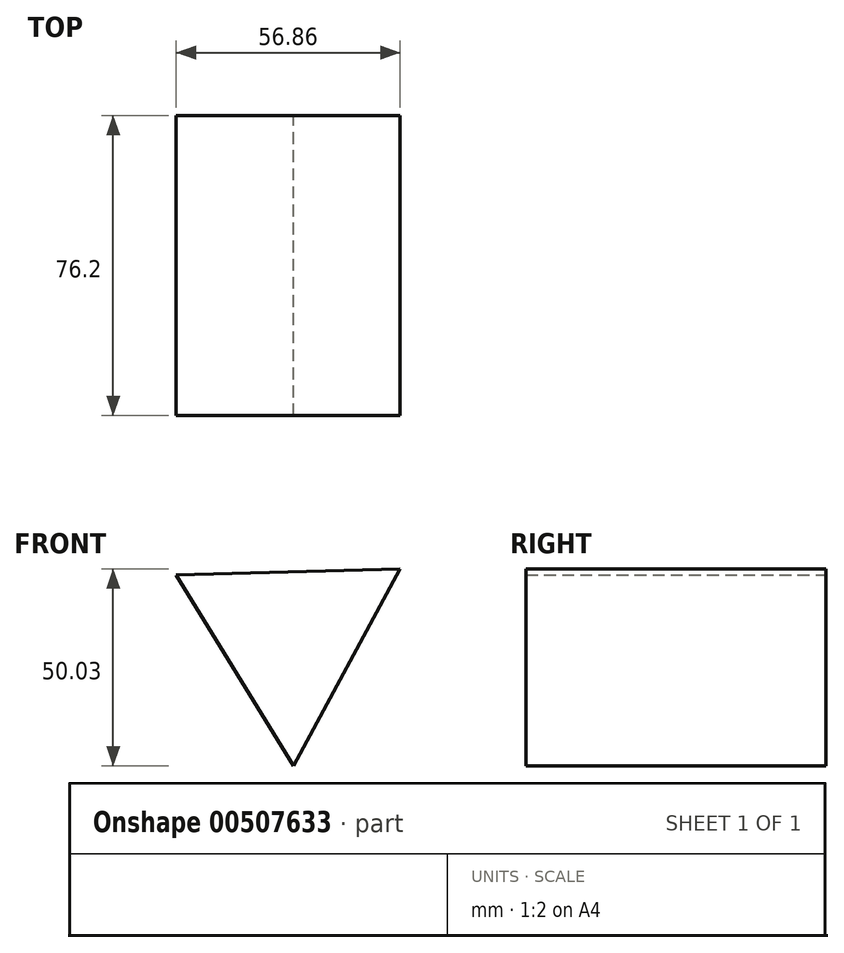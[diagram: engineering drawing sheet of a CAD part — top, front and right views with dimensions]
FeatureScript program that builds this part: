
annotation { "Feature Type Name" : "Feature", "Feature Type Description" : "" }
export const myFeature = defineFeature(function(context is Context, id is Id, definition is map)
    precondition{}
    {
        {
            var Q0;
            Q0=qCreatedBy(makeId("Front.planeOp"),FACE);
            var sketch = newSketch(context, id + "F0", { "sketchPlane" : qUnion([Q0])});
            skCircle(sketch, "E0.cCircle", {"center": v(0, 0) * mm, "radius": 16.42 * mm, "construction": true});
            skLineSegment(sketch, "E0.0", {"start": v(0.9, -32.83) * mm, "end": v(-28.88, 15.63) * mm});
            skLineSegment(sketch, "E0.1", {"start": v(-28.88, 15.63) * mm, "end": v(27.98, 17.2) * mm});
            skLineSegment(sketch, "E0.2", {"start": v(27.98, 17.2) * mm, "end": v(0.9, -32.83) * mm});
            skPoint(sketch, "E0.0.midPoint", {"position": v(-14, -8.6) * mm});
            skSolve(sketch);
        }
        {
            var Q0;
            Q0=makeQuery(id+"F0.imprint","IMPRINT",FACE,{"disambiguationData":[TD([[makeQuery(id+"F0.imprint","IMPRINT",EDGE,{"derivedFrom":sQuery(id+"F0.wireOp",EDGE,"E0.0")}),-1.0]])]});
            extrude(context, id + "F1", {"entities" : qUnion([Q0]), "endBound" : BoundingType.SYMMETRIC, "depth" : 76.2 * mm});
        }
    });
